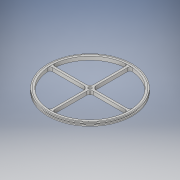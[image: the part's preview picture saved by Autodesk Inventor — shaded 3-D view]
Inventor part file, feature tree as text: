
AUTODESK INVENTOR PART (.ipt)
format: ipt  version: 2018 (Build 220112000, 112)  size: 424,960 bytes
history: native  units: in
note: dims shown in document units (in); Inventor stores cm internally (conversion verified against a paired STEP export)
features: extrude x7, sketch x7, fillet x2
ambient origin geometry x8: Origin, YZ Plane, XZ Plane, XY Plane, X Axis, Y Axis, Z Axis, Center Point
bodies: Solid1 (feature_tree)
feature tree (16):
  extrude  "Extrusion1"  Depth=4.849in
  extrude  "Extrusion2"  Depth=0.0625in
  extrude  "Extrusion3"  Depth=0.0625in TaperAngle=0.0deg
  extrude  "Extrusion4"  Depth=0.204in
  extrude  "Extrusion5"  Depth=0.204in
  extrude  "Extrusion6"  Depth=0.125in
  extrude  "Extrusion7"  Depth=0.204in TaperAngle=0.0deg
  fillet  "Fillet1"  Radius=0.125in
  fillet  "Fillet2"  Radius=0.125in
  sketch  "Sketch1"  dims[d0=4.7244in d1=4.849in]
  sketch  "Sketch2"  dims[d2=0.0625in d3=0.0in d4=4.5in]
  sketch  "Sketch3"  dims[d5=0.0787in d6=0.0in d7=0.0625in d8=0.0in]
  sketch  "Sketch4"  dims[d9=0.204in d10=0.0in d11=4.5in]
  sketch  "Sketch5"  dims[d12=0.204in d13=0.0in d14=0.195in]
  sketch  "Sketch6"  dims[d15=0.204in d16=0.0in d17=0.125in]
  sketch  "Sketch7"  dims[d18=0.125in d19=0.204in d20=0.0in d21=0.125in d22=0.125in]
